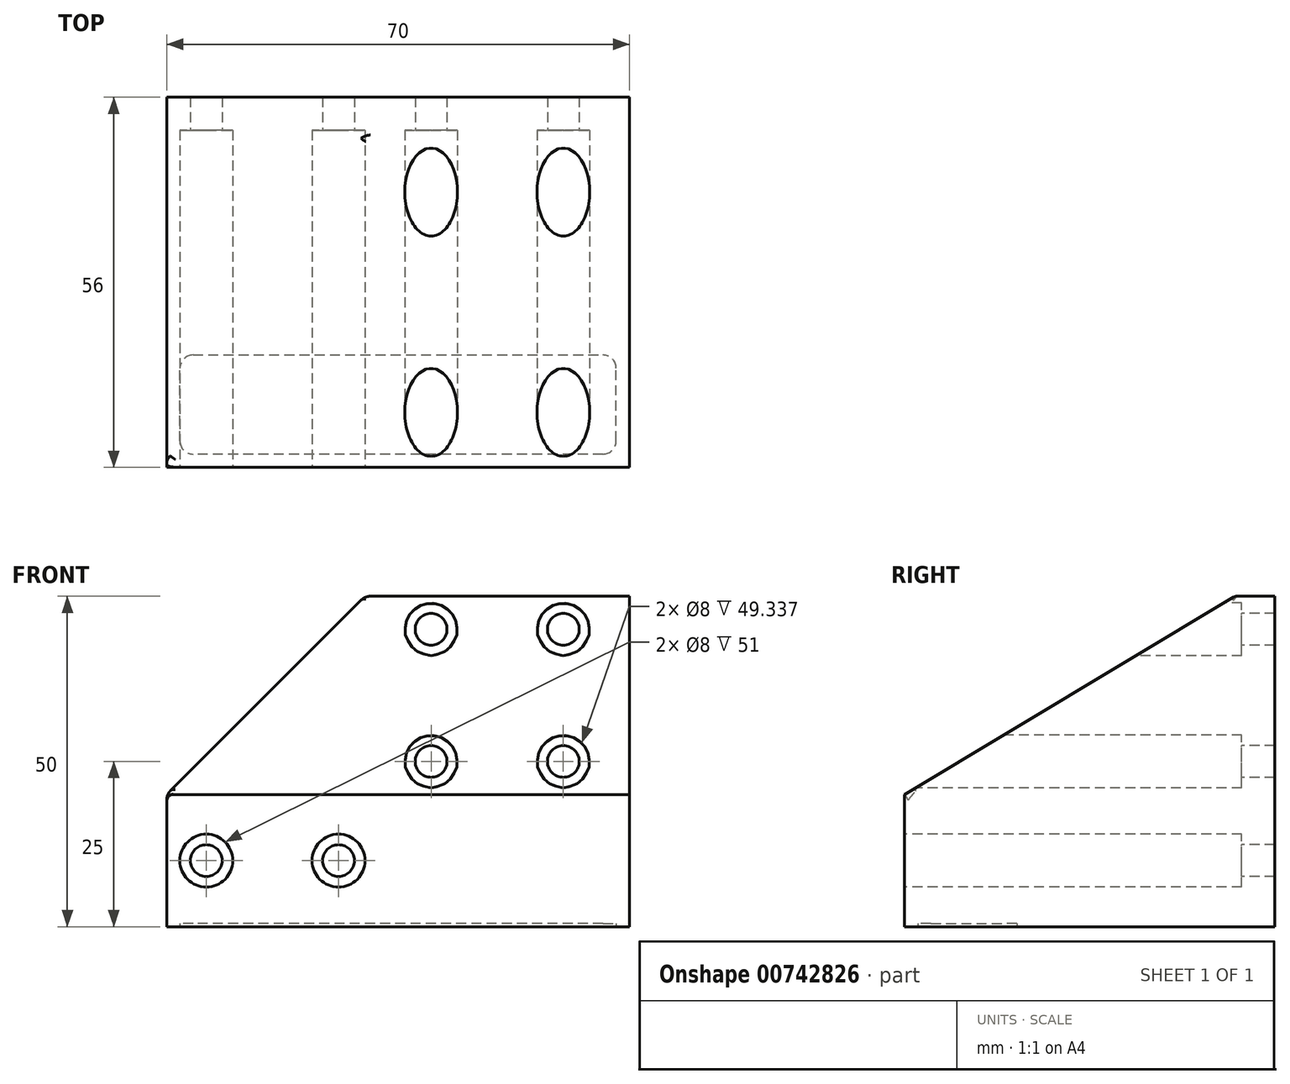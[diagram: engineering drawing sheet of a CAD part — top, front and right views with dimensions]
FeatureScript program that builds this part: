
annotation { "Feature Type Name" : "Feature", "Feature Type Description" : "" }
export const myFeature = defineFeature(function(context is Context, id is Id, definition is map)
    precondition{}
    {
        {
            var Q0;
            Q0=qCreatedBy(makeId("Front.planeOp"),FACE);
            var sketch = newSketch(context, id + "F0", { "sketchPlane" : qUnion([Q0])});
            skLineSegment(sketch, "E0.bottom", {"start": v(0, 0) * mm, "end": v(-70, 0) * mm});
            skLineSegment(sketch, "E0.top", {"start": v(0, 50) * mm, "end": v(-70, 50) * mm});
            skLineSegment(sketch, "E0.left", {"start": v(0, 0) * mm, "end": v(0, 50) * mm});
            skLineSegment(sketch, "E0.right", {"start": v(-70, 0) * mm, "end": v(-70, 50) * mm});
            skSolve(sketch);
        }
        {
            var Q0;
            Q0=makeQuery(id+"F0.imprint","IMPRINT",FACE,{"disambiguationData":[TD([[makeQuery(id+"F0.imprint","IMPRINT",EDGE,{"derivedFrom":sQuery(id+"F0.wireOp",EDGE,"E0.bottom")}),-1.0]])]});
            extrude(context, id + "F1", {"entities" : qUnion([Q0]), "depth" : 56 * mm});
        }
        {
            var Q0;
            Q0=makeQuery(id+"F1.opExtrude","SWEPT_EDGE",EDGE,{"disambiguationData":[OSD([sQuery(id+"F0.wireOp",EDGE,"E0.top"),sQuery(id+"F0.wireOp",EDGE,"E0.right")])]});
            chamfer(context, id + "F2", {"entities" : qUnion([Q0]), "width" : 30 * mm, "tangentPropagation" : true});
        }
        {
            var Q0;
            Q0=qCreatedBy(makeId("Right.planeOp"),FACE);
            var sketch = newSketch(context, id + "F3", { "sketchPlane" : qUnion([Q0])});
            skLineSegment(sketch, "E1", {"start": v(-6, 50) * mm, "end": v(-56, 20) * mm});
            skLineSegment(sketch, "E2", {"start": v(-56, 20) * mm, "end": v(-56, 50) * mm});
            skLineSegment(sketch, "E3", {"start": v(-56, 50) * mm, "end": v(-6, 50) * mm});
            skSolve(sketch);
        }
        {
            var Q0;
            Q0=qSketchRegion(id+"F3",true);
            extrude(context, id + "F4", {"entities" : qUnion([Q0]), "operationType" : NewBodyOperationType.REMOVE, "endBound" : BoundingType.THROUGH_ALL, "oppositeDirection" : true, "depth" : 25 * mm});
        }
        {
            var Q0;
            Q0=qCreatedBy(makeId("Front.planeOp"),FACE);
            cPlane(context, id + "F5", {"entities" : qUnion([Q0]), "cplaneType" : CPlaneType.OFFSET, "offset" : 56 * mm, "width" : 150 * mm, "height" : 150 * mm});
        }
        {
            var Q0;
            Q0=qCreatedBy(id+"F5.planeOp",FACE);
            var sketch = newSketch(context, id + "F6", { "sketchPlane" : qUnion([Q0])});
            skLineSegment(sketch, "E4", {"start": v(-64, 10) * mm, "end": v(-44, 10) * mm});
            skLineSegment(sketch, "E5", {"start": v(-64, 10) * mm, "end": v(-70, 10) * mm, "construction": true});
            skLineSegment(sketch, "E6.bottom", {"start": v(-30, 45) * mm, "end": v(-10, 45) * mm});
            skLineSegment(sketch, "E6.top", {"start": v(-30, 25) * mm, "end": v(-10, 25) * mm});
            skLineSegment(sketch, "E6.left", {"start": v(-30, 45) * mm, "end": v(-30, 25) * mm});
            skLineSegment(sketch, "E6.right", {"start": v(-10, 45) * mm, "end": v(-10, 25) * mm});
            skSolve(sketch);
        }
        {
            var Q0;
            Q0=sQuery(id+"F6.wireOp",VERTEX,"E4.start");
            var Q1;
            Q1=sQuery(id+"F6.wireOp",VERTEX,"E4.end");
            var Q2;
            Q2=sQuery(id+"F6.wireOp",VERTEX,"E6.bottom.start");
            var Q3;
            Q3=sQuery(id+"F6.wireOp",VERTEX,"E6.top.start");
            var Q4;
            Q4=sQuery(id+"F6.wireOp",VERTEX,"E6.bottom.end");
            var Q5;
            Q5=sQuery(id+"F6.wireOp",VERTEX,"E6.top.end");
            var Q6;
            Q6=makeQuery(id+"F1.opExtrude","SWEPT_BODY",BODY,{"disambiguationData":[OSD([sQuery(id+"F0.wireOp",EDGE,"E0.bottom"),sQuery(id+"F0.wireOp",EDGE,"E0.top"),sQuery(id+"F0.wireOp",EDGE,"E0.left"),sQuery(id+"F0.wireOp",EDGE,"E0.right")])]});
            hole(context, id + "F7", {"style" : HoleStyle.C_BORE, "endStyle" : HoleEndStyle.THROUGH, "holeDiameter" : 4.8 * mm, "cBoreDiameter" : 8 * mm, "cBoreDepth" : 51 * mm, "isTappedThrough" : true, "tappedDepth" : 12 * mm, "tapClearance" : 3, "startFromSketch" : true, "locations" : qUnion([Q0, Q1, Q2, Q3, Q4, Q5]), "scope" : qUnion([Q6])});
        }
        {
            var Q0;
            {var subQ0=sQuery(id+"F0.wireOp",EDGE,"E0.right");Q0=makeQuery(id+"F2.opChamfer","BLEND_EDGE",EDGE,{"blendedFrom":[makeQuery(id+"F1.opExtrude","SWEPT_EDGE",EDGE,{"disambiguationData":[OSD([sQuery(id+"F0.wireOp",EDGE,"E0.top"),subQ0])]}),makeQuery(id+"F1.opExtrude","SWEPT_FACE",FACE,{"disambiguationData":[OSD([subQ0])]})],"blendedInto":[makeQuery(id+"F1.opExtrude","SWEPT_FACE",FACE,{"disambiguationData":[OSD([subQ0])]})]});}
            var Q1;
            Q1=makeQuery(id+"F4.boolean.opBoolean","COPY",EDGE,{"derivedFrom":makeQuery(id+"F4.opExtrude","SWEPT_EDGE",EDGE,{"disambiguationData":[OSD([sQuery(id+"F3.wireOp",EDGE,"E1"),sQuery(id+"F3.wireOp",EDGE,"E2")])]})});
            var Q2;
            {var subQ0=sQuery(id+"F0.wireOp",EDGE,"E0.top");Q2=makeQuery(id+"F2.opChamfer","BLEND_EDGE",EDGE,{"blendedFrom":[makeQuery(id+"F1.opExtrude","SWEPT_EDGE",EDGE,{"disambiguationData":[OSD([subQ0,sQuery(id+"F0.wireOp",EDGE,"E0.right")])]}),makeQuery(id+"F1.opExtrude","SWEPT_FACE",FACE,{"disambiguationData":[OSD([subQ0])]})],"blendedInto":[makeQuery(id+"F1.opExtrude","SWEPT_FACE",FACE,{"disambiguationData":[OSD([subQ0])]})]});}
            var Q3;
            Q3=makeQuery(id+"F4.boolean.opBoolean","COPY",EDGE,{"derivedFrom":makeQuery(id+"F4.opExtrude","SWEPT_EDGE",EDGE,{"disambiguationData":[OSD([sQuery(id+"F3.wireOp",EDGE,"E1"),sQuery(id+"F3.wireOp",EDGE,"E3")])]})});
            fillet(context, id + "F8", {"entities" : qUnion([Q0, Q1, Q2, Q3]), "radius" : 2 * mm, "tangentPropagation" : true, "allowEdgeOverflow" : false});
        }
        {
            var Q0;
            Q0=makeQuery(id+"F4.boolean.opBoolean","INTERSECT",EDGE,{"derivedFrom":[makeQuery(id+"F2.opChamfer","BLEND_FACE",FACE,{"disambiguationData":[OSD([sQuery(id+"F0.wireOp",EDGE,"E0.top"),sQuery(id+"F0.wireOp",EDGE,"E0.right")])]}),makeQuery(id+"F4.opExtrude","SWEPT_FACE",FACE,{"disambiguationData":[OSD([sQuery(id+"F3.wireOp",EDGE,"E1")])]})]});
            var Q1;
            Q1=makeQuery(id+"F4.boolean.opBoolean","COPY",EDGE,{"derivedFrom":makeQuery(id+"F4.opExtrude","CAP_EDGE",EDGE,{"disambiguationData":[OSD([sQuery(id+"F3.wireOp",EDGE,"E1")])],"isStart":true})});
            fillet(context, id + "F9", {"entities" : qUnion([Q0, Q1]), "radius" : 1 * mm, "tangentPropagation" : true, "allowEdgeOverflow" : false});
        }
        {
            var Q0;
            Q0=makeQuery(id+"F1.opExtrude","SWEPT_FACE",FACE,{"disambiguationData":[OSD([sQuery(id+"F0.wireOp",EDGE,"E0.bottom")])]});
            var sketch = newSketch(context, id + "F10", { "sketchPlane" : qUnion([Q0])});
            skLineSegment(sketch, "E7.0", {"start": v(-68, 54) * mm, "end": v(-68, 39) * mm});
            skLineSegment(sketch, "E7.1", {"start": v(-2, 54) * mm, "end": v(-68, 54) * mm});
            skLineSegment(sketch, "E7.2", {"start": v(-2, 54) * mm, "end": v(-2, 39) * mm});
            skLineSegment(sketch, "E8", {"start": v(-68, 39) * mm, "end": v(-2, 39) * mm});
            skSolve(sketch);
        }
        {
            var Q0;
            Q0=makeQuery(id+"F10.imprint","IMPRINT",FACE,{"disambiguationData":[TD([[makeQuery(id+"F10.imprint","IMPRINT",EDGE,{"derivedFrom":sQuery(id+"F10.wireOp",EDGE,"E7.0")}),1.0]])]});
            extrude(context, id + "F11", {"entities" : qUnion([Q0]), "operationType" : NewBodyOperationType.REMOVE, "oppositeDirection" : true, "depth" : 0.5 * mm});
        }
        {
            var Q0;
            Q0=makeQuery(id+"F11.boolean.opBoolean","COPY",EDGE,{"derivedFrom":makeQuery(id+"F11.opExtrude","SWEPT_EDGE",EDGE,{"disambiguationData":[OSD([sQuery(id+"F10.wireOp",EDGE,"E7.1"),sQuery(id+"F10.wireOp",EDGE,"E7.2")])]})});
            var Q1;
            Q1=makeQuery(id+"F11.boolean.opBoolean","COPY",EDGE,{"derivedFrom":makeQuery(id+"F11.opExtrude","SWEPT_EDGE",EDGE,{"disambiguationData":[OSD([sQuery(id+"F10.wireOp",EDGE,"E7.0"),sQuery(id+"F10.wireOp",EDGE,"E7.1")])]})});
            var Q2;
            Q2=makeQuery(id+"F11.boolean.opBoolean","COPY",EDGE,{"derivedFrom":makeQuery(id+"F11.opExtrude","SWEPT_EDGE",EDGE,{"disambiguationData":[OSD([sQuery(id+"F10.wireOp",EDGE,"E7.0"),sQuery(id+"F10.wireOp",EDGE,"E8")])]})});
            var Q3;
            Q3=makeQuery(id+"F11.boolean.opBoolean","COPY",EDGE,{"derivedFrom":makeQuery(id+"F11.opExtrude","SWEPT_EDGE",EDGE,{"disambiguationData":[OSD([sQuery(id+"F10.wireOp",EDGE,"E7.2"),sQuery(id+"F10.wireOp",EDGE,"E8")])]})});
            fillet(context, id + "F12", {"entities" : qUnion([Q0, Q1, Q2, Q3]), "radius" : 2 * mm, "tangentPropagation" : true, "allowEdgeOverflow" : false});
        }
    });
